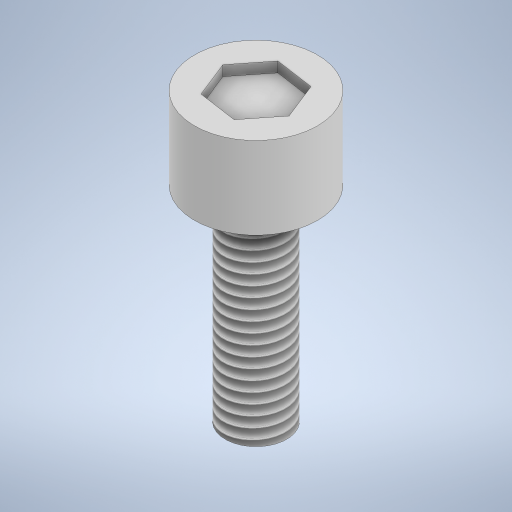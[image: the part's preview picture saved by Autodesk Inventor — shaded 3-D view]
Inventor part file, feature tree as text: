
AUTODESK INVENTOR PART (.ipt)
format: ipt  version: 2024 (Build 280153000, 153)  size: 278,016 bytes
history: native  units: mm
features: extrude x3, sketch x3, thread x1
ambient origin geometry x8: Origin, YZ Plane, XZ Plane, XY Plane, X Axis, Y Axis, Z Axis, Center Point
bodies: Solid1 (feature_tree)
feature tree (7):
  extrude  "Extrusion1"  Depth=10.0mm TaperAngle=0.0deg
  extrude  "Extrusion2"  Depth=4.0mm TaperAngle=0.0deg
  extrude  "Extrusion3"  Depth=10.0mm TaperAngle=0.0deg
  thread  "Thread1"  [1 undecoded]
  sketch  "Sketch1"  dims[d0=3.0mm d1=10.0mm d2=0.0mm]
  sketch  "Sketch2"  dims[d3=6.0mm d4=4.0mm d5=0.0mm]
  sketch  "Sketch3"  dims[d6=0.5mm d7=0.0mm d8=10.0mm d9=0.0mm]
note: 1 required parameter value undecoded (feature->parameter linkage not recoverable at this tier; creation-order binding heuristic only, values carry confidence <= 0.55)
